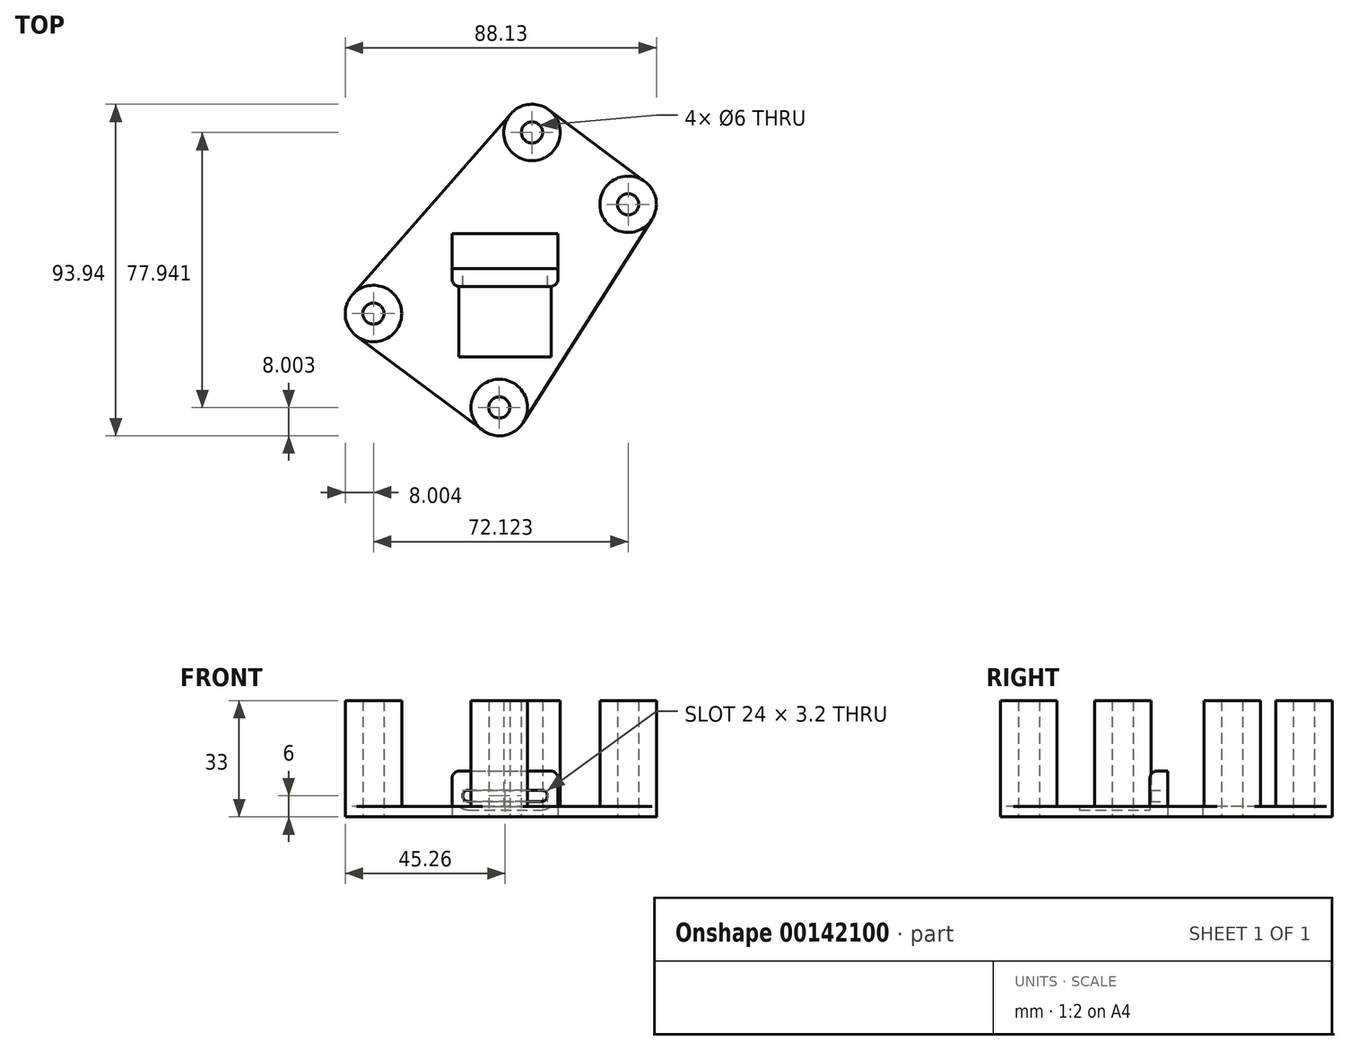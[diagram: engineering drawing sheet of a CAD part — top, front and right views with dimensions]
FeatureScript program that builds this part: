
annotation { "Feature Type Name" : "Feature", "Feature Type Description" : "" }
export const myFeature = defineFeature(function(context is Context, id is Id, definition is map)
    precondition{}
    {
        {
            var Q0;
            Q0=qCreatedBy(makeId("Top.planeOp"),FACE);
            var sketch = newSketch(context, id + "F0", { "sketchPlane" : qUnion([Q0])});
            skCircle(sketch, "E0", {"center": v(7.63, 38.61) * mm, "radius": 3 * mm});
            skCircle(sketch, "E1", {"center": v(34.87, 18.26) * mm, "radius": 3 * mm});
            skCircle(sketch, "E2", {"center": v(-37.26, -12.7) * mm, "radius": 3 * mm});
            skCircle(sketch, "E3", {"center": v(-1.62, -39.33) * mm, "radius": 3 * mm});
            skCircle(sketch, "E4", {"center": v(-37.26, -12.7) * mm, "radius": 8 * mm});
            skCircle(sketch, "E5", {"center": v(-1.62, -39.33) * mm, "radius": 8 * mm});
            skCircle(sketch, "E6", {"center": v(34.87, 18.26) * mm, "radius": 8 * mm});
            skCircle(sketch, "E7", {"center": v(7.63, 38.61) * mm, "radius": 8 * mm});
            skLineSegment(sketch, "E8", {"start": v(-15, 0) * mm, "end": v(15, 0) * mm});
            skLineSegment(sketch, "E9", {"start": v(-15, 0) * mm, "end": v(-15, 10) * mm});
            skLineSegment(sketch, "E10", {"start": v(-15, 10) * mm, "end": v(15, 10) * mm});
            skLineSegment(sketch, "E11", {"start": v(15, 10) * mm, "end": v(15, 0) * mm});
            skLineSegment(sketch, "E12", {"start": v(1.6, 43.88) * mm, "end": v(-43.28, -7.43) * mm});
            skLineSegment(sketch, "E13", {"start": v(12.42, 45.02) * mm, "end": v(39.66, 24.67) * mm});
            skLineSegment(sketch, "E14", {"start": v(-42.04, -19.1) * mm, "end": v(-6.4, -45.74) * mm});
            skLineSegment(sketch, "E15", {"start": v(5.14, -43.6) * mm, "end": v(41.63, 13.98) * mm});
            skSolve(sketch);
        }
        {
            var Q0;
            Q0=makeQuery(id+"F0.imprint","IMPRINT",FACE,{"disambiguationData":[TD([[makeQuery(id+"F0.imprint","IMPRINT",EDGE,{"derivedFrom":sQuery(id+"F0.wireOp",EDGE,"E8")}),-1.0]])]});
            var Q1;
            Q1=makeQuery(id+"F0.imprint","IMPRINT",FACE,{"disambiguationData":[TD([[makeQuery(id+"F0.imprint","IMPRINT",EDGE,{"derivedFrom":sQuery(id+"F0.wireOp",EDGE,"E2")}),-1.0]])]});
            var Q2;
            Q2=makeQuery(id+"F0.imprint","IMPRINT",FACE,{"disambiguationData":[TD([[makeQuery(id+"F0.imprint","IMPRINT",EDGE,{"derivedFrom":sQuery(id+"F0.wireOp",EDGE,"E0")}),-1.0]])]});
            var Q3;
            Q3=makeQuery(id+"F0.imprint","IMPRINT",FACE,{"disambiguationData":[TD([[makeQuery(id+"F0.imprint","IMPRINT",EDGE,{"derivedFrom":sQuery(id+"F0.wireOp",EDGE,"E1")}),-1.0]])]});
            var Q4;
            Q4=makeQuery(id+"F0.imprint","IMPRINT",FACE,{"disambiguationData":[TD([[makeQuery(id+"F0.imprint","IMPRINT",EDGE,{"derivedFrom":sQuery(id+"F0.wireOp",EDGE,"E3")}),-1.0]])]});
            extrude(context, id + "F1", {"entities" : qUnion([Q0, Q1, Q2, Q3, Q4]), "depth" : 3 * mm});
        }
        {
            var Q0;
            Q0=makeQuery(id+"F1.opExtrude","CAP_FACE",FACE,{"disambiguationData":[OSD([sQuery(id+"F0.wireOp",EDGE,"E0"),sQuery(id+"F0.wireOp",EDGE,"E1"),sQuery(id+"F0.wireOp",EDGE,"E2"),sQuery(id+"F0.wireOp",EDGE,"E3"),sQuery(id+"F0.wireOp",EDGE,"E4"),sQuery(id+"F0.wireOp",EDGE,"E5"),sQuery(id+"F0.wireOp",EDGE,"E6"),sQuery(id+"F0.wireOp",EDGE,"E7"),sQuery(id+"F0.wireOp",EDGE,"E8"),sQuery(id+"F0.wireOp",EDGE,"E9"),sQuery(id+"F0.wireOp",EDGE,"E10"),sQuery(id+"F0.wireOp",EDGE,"E11"),sQuery(id+"F0.wireOp",EDGE,"E12"),sQuery(id+"F0.wireOp",EDGE,"E13"),sQuery(id+"F0.wireOp",EDGE,"E14"),sQuery(id+"F0.wireOp",EDGE,"E15")])],"isStart":false});
            var sketch = newSketch(context, id + "F2", { "sketchPlane" : qUnion([Q0])});
            skCircle(sketch, "E16", {"center": v(7.63, 38.61) * mm, "radius": 8 * mm});
            skCircle(sketch, "E17", {"center": v(34.87, 18.26) * mm, "radius": 8 * mm});
            skCircle(sketch, "E18", {"center": v(-37.26, -12.7) * mm, "radius": 8 * mm});
            skCircle(sketch, "E19", {"center": v(-1.62, -39.33) * mm, "radius": 8 * mm});
            skSolve(sketch);
        }
        {
            var Q0;
            Q0=makeQuery(id+"F2.imprint","IMPRINT",FACE,{"disambiguationData":[TD([[makeQuery(id+"F2.imprint","IMPRINT",EDGE,{"derivedFrom":makeQuery(id+"F1.opExtrude","CAP_EDGE",EDGE,{"disambiguationData":[OSD([sQuery(id+"F0.wireOp",EDGE,"E0")])],"isStart":false})}),-1.0]])]});
            var Q1;
            Q1=makeQuery(id+"F2.imprint","IMPRINT",FACE,{"disambiguationData":[TD([[makeQuery(id+"F2.imprint","IMPRINT",EDGE,{"derivedFrom":makeQuery(id+"F1.opExtrude","CAP_EDGE",EDGE,{"disambiguationData":[OSD([sQuery(id+"F0.wireOp",EDGE,"E2")])],"isStart":false})}),-1.0]])]});
            var Q2;
            Q2=makeQuery(id+"F2.imprint","IMPRINT",FACE,{"disambiguationData":[TD([[makeQuery(id+"F2.imprint","IMPRINT",EDGE,{"derivedFrom":makeQuery(id+"F1.opExtrude","CAP_EDGE",EDGE,{"disambiguationData":[OSD([sQuery(id+"F0.wireOp",EDGE,"E1")])],"isStart":false})}),-1.0]])]});
            var Q3;
            Q3=makeQuery(id+"F2.imprint","IMPRINT",FACE,{"disambiguationData":[TD([[makeQuery(id+"F2.imprint","IMPRINT",EDGE,{"derivedFrom":makeQuery(id+"F1.opExtrude","CAP_EDGE",EDGE,{"disambiguationData":[OSD([sQuery(id+"F0.wireOp",EDGE,"E3")])],"isStart":false})}),-1.0]])]});
            extrude(context, id + "F3", {"entities" : qUnion([Q0, Q1, Q2, Q3]), "operationType" : NewBodyOperationType.ADD, "depth" : 30 * mm});
        }
        {
            var Q0;
            Q0=makeQuery(id+"F1.opExtrude","CAP_FACE",FACE,{"disambiguationData":[OSD([sQuery(id+"F0.wireOp",EDGE,"E0"),sQuery(id+"F0.wireOp",EDGE,"E1"),sQuery(id+"F0.wireOp",EDGE,"E2"),sQuery(id+"F0.wireOp",EDGE,"E3"),sQuery(id+"F0.wireOp",EDGE,"E4"),sQuery(id+"F0.wireOp",EDGE,"E5"),sQuery(id+"F0.wireOp",EDGE,"E6"),sQuery(id+"F0.wireOp",EDGE,"E7"),sQuery(id+"F0.wireOp",EDGE,"E8"),sQuery(id+"F0.wireOp",EDGE,"E9"),sQuery(id+"F0.wireOp",EDGE,"E10"),sQuery(id+"F0.wireOp",EDGE,"E11"),sQuery(id+"F0.wireOp",EDGE,"E12"),sQuery(id+"F0.wireOp",EDGE,"E13"),sQuery(id+"F0.wireOp",EDGE,"E14"),sQuery(id+"F0.wireOp",EDGE,"E15")])],"isStart":false});
            var sketch = newSketch(context, id + "F4", { "sketchPlane" : qUnion([Q0])});
            skLineSegment(sketch, "E20.bottom", {"start": v(-15, 0) * mm, "end": v(15, 0) * mm});
            skLineSegment(sketch, "E20.top", {"start": v(-15, -5) * mm, "end": v(15, -5) * mm});
            skLineSegment(sketch, "E20.left", {"start": v(-15, 0) * mm, "end": v(-15, -5) * mm});
            skLineSegment(sketch, "E20.right", {"start": v(15, 0) * mm, "end": v(15, -5) * mm});
            skSolve(sketch);
        }
        {
            var Q0;
            Q0=makeQuery(id+"F4.imprint","IMPRINT",FACE,{"disambiguationData":[TD([[makeQuery(id+"F4.imprint","IMPRINT",EDGE,{"derivedFrom":sQuery(id+"F4.wireOp",EDGE,"E20.bottom")}),-1.0]])]});
            extrude(context, id + "F5", {"entities" : qUnion([Q0]), "operationType" : NewBodyOperationType.ADD, "depth" : 10 * mm});
        }
        {
            var Q0;
            Q0=makeQuery(id+"F5.boolean.opBoolean","MERGE",FACE,{"derivedFrom":[makeQuery(id+"F1.opExtrude","SWEPT_FACE",FACE,{"disambiguationData":[OSD([sQuery(id+"F0.wireOp",EDGE,"E8")])]}),makeQuery(id+"F5.opExtrude","SWEPT_FACE",FACE,{"disambiguationData":[OSD([sQuery(id+"F4.wireOp",EDGE,"E20.bottom")])]})]});
            var sketch = newSketch(context, id + "F6", { "sketchPlane" : qUnion([Q0])});
            skArc(sketch, "E21", {"start": v(-10.4, 7.6) * mm, "mid": v(-12, 6) * mm, "end": v(-10.4, 4.4) * mm});
            skArc(sketch, "E22", {"start": v(10.4, 4.4) * mm, "mid": v(12, 6) * mm, "end": v(10.4, 7.6) * mm});
            skLineSegment(sketch, "E23", {"start": v(-10.4, 7.6) * mm, "end": v(10.4, 7.6) * mm});
            skLineSegment(sketch, "E24", {"start": v(-10.4, 4.4) * mm, "end": v(10.4, 4.4) * mm});
            skSolve(sketch);
        }
        {
            var Q0;
            Q0=makeQuery(id+"F6.imprint","IMPRINT",FACE,{"disambiguationData":[TD([[makeQuery(id+"F6.imprint","IMPRINT",EDGE,{"derivedFrom":sQuery(id+"F6.wireOp",EDGE,"E21")}),1.0]])]});
            extrude(context, id + "F7", {"entities" : qUnion([Q0]), "operationType" : NewBodyOperationType.REMOVE, "endBound" : BoundingType.UP_TO_NEXT, "oppositeDirection" : true, "depth" : 25 * mm});
        }
        {
            var Q0;
            Q0=makeQuery(id+"F5.opExtrude","SWEPT_EDGE",EDGE,{"disambiguationData":[OSD([sQuery(id+"F4.wireOp",EDGE,"E20.top"),sQuery(id+"F4.wireOp",EDGE,"E20.right")])]});
            var Q1;
            Q1=makeQuery(id+"F5.opExtrude","CAP_EDGE",EDGE,{"disambiguationData":[OSD([sQuery(id+"F4.wireOp",EDGE,"E20.right")])],"isStart":false});
            var Q2;
            Q2=makeQuery(id+"F5.opExtrude","CAP_EDGE",EDGE,{"disambiguationData":[OSD([sQuery(id+"F4.wireOp",EDGE,"E20.top")])],"isStart":false});
            var Q3;
            Q3=makeQuery(id+"F5.opExtrude","SWEPT_EDGE",EDGE,{"disambiguationData":[OSD([sQuery(id+"F4.wireOp",EDGE,"E20.top"),sQuery(id+"F4.wireOp",EDGE,"E20.left")])]});
            var Q4;
            Q4=makeQuery(id+"F5.opExtrude","CAP_EDGE",EDGE,{"disambiguationData":[OSD([sQuery(id+"F4.wireOp",EDGE,"E20.left")])],"isStart":false});
            fillet(context, id + "F8", {"entities" : qUnion([Q0, Q1, Q2, Q3, Q4]), "radius" : 2 * mm, "tangentPropagation" : true, "allowEdgeOverflow" : false});
        }
        {
            var Q0;
            Q0=makeQuery(id+"F5.opExtrude","SWEPT_FACE",FACE,{"disambiguationData":[OSD([sQuery(id+"F4.wireOp",EDGE,"E20.top")])]});
            var sketch = newSketch(context, id + "F9", { "sketchPlane" : qUnion([Q0])});
            skArc(sketch, "E25", {"start": v(-10.4, 10) * mm, "mid": v(-14.4, 6) * mm, "end": v(-10.4, 2) * mm});
            skArc(sketch, "E26", {"start": v(10.4, 2) * mm, "mid": v(14.4, 6) * mm, "end": v(10.4, 10) * mm});
            skLineSegment(sketch, "E27", {"start": v(-10.4, 10) * mm, "end": v(10.4, 10) * mm});
            skLineSegment(sketch, "E28", {"start": v(-10.4, 2) * mm, "end": v(10.4, 2) * mm});
            skSolve(sketch);
        }
        {
            var Q0;
            {var subQ2=sQuery(id+"F9.wireOp",EDGE,"E27");Q0=makeQuery(id+"F9.imprint","IMPRINT",FACE,{"disambiguationData":[TD([[makeQuery(id+"F9.imprint","IMPRINT",EDGE,{"derivedFrom":subQ2}),-1.0]])]});}
            var Q1;
            {var subQ2=sQuery(id+"F9.wireOp",EDGE,"E28");Q1=makeQuery(id+"F9.imprint","IMPRINT",FACE,{"disambiguationData":[TD([[makeQuery(id+"F9.imprint","IMPRINT",EDGE,{"derivedFrom":subQ2}),1.0]])]});}
            extrude(context, id + "F10", {"entities" : qUnion([Q0, Q1]), "operationType" : NewBodyOperationType.REMOVE, "depth" : 20 * mm});
        }
    });
